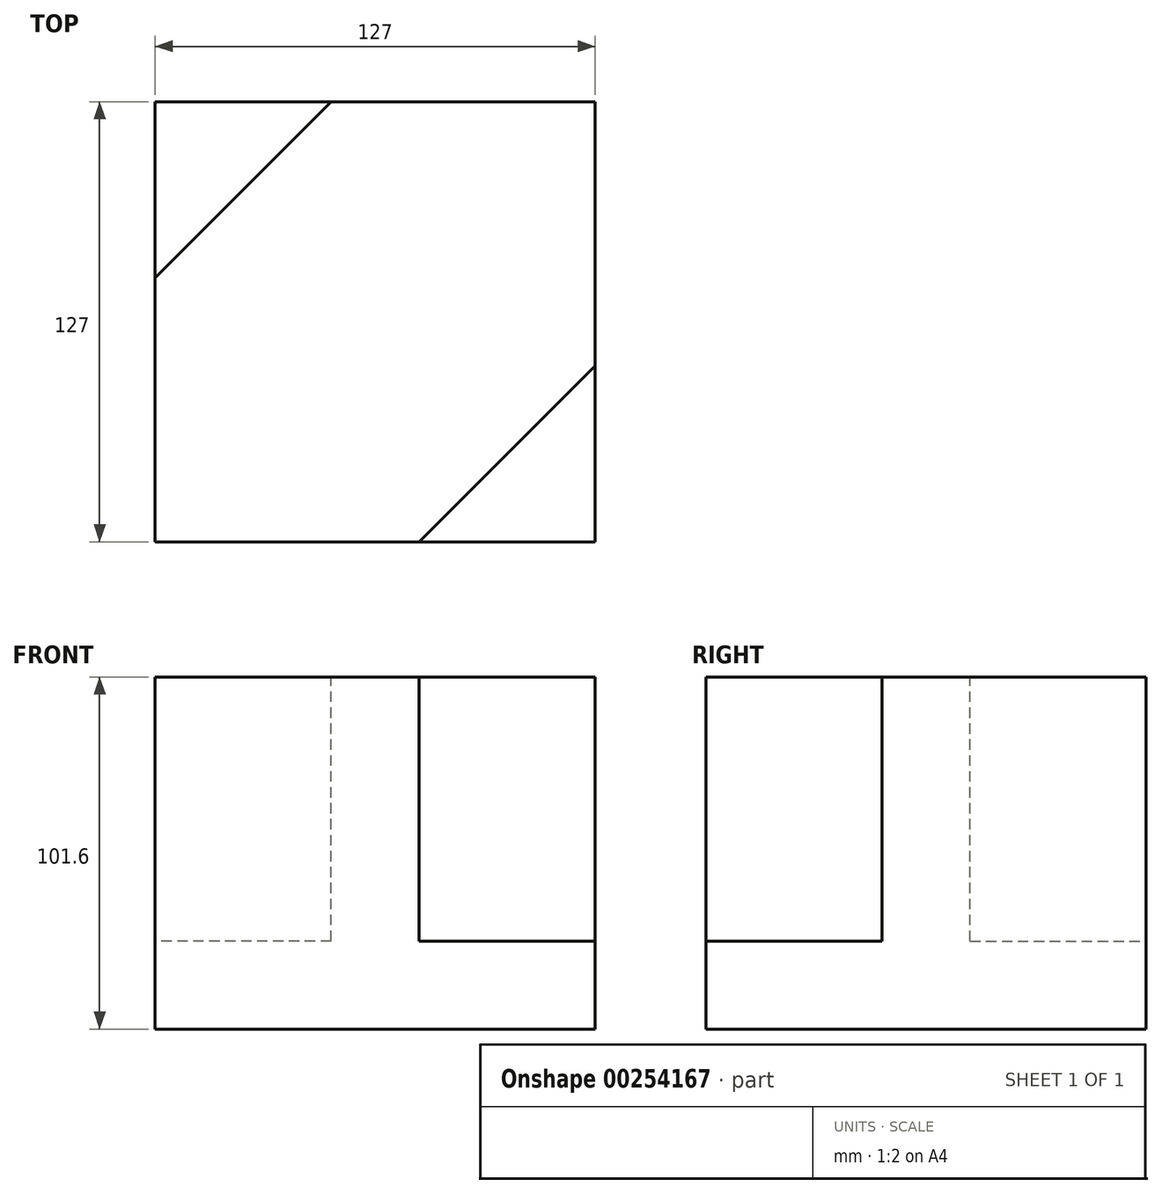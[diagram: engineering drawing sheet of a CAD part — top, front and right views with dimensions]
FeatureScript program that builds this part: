
annotation { "Feature Type Name" : "Feature", "Feature Type Description" : "" }
export const myFeature = defineFeature(function(context is Context, id is Id, definition is map)
    precondition{}
    {
        {
            var Q0;
            Q0=qCreatedBy(makeId("Front.planeOp"),FACE);
            var sketch = newSketch(context, id + "F0", { "sketchPlane" : qUnion([Q0])});
            skLineSegment(sketch, "E0.bottom", {"start": v(63.5, -50.8) * mm, "end": v(-63.5, -50.8) * mm});
            skLineSegment(sketch, "E0.top", {"start": v(63.5, 50.8) * mm, "end": v(-63.5, 50.8) * mm});
            skLineSegment(sketch, "E0.left", {"start": v(63.5, -50.8) * mm, "end": v(63.5, 50.8) * mm});
            skLineSegment(sketch, "E0.right", {"start": v(-63.5, -50.8) * mm, "end": v(-63.5, 50.8) * mm});
            skPoint(sketch, "E0.middle", {"position": v(0, 0) * mm});
            skSolve(sketch);
        }
        {
            var Q0;
            Q0=makeQuery(id+"F0.imprint","IMPRINT",FACE,{"disambiguationData":[TD([[makeQuery(id+"F0.imprint","IMPRINT",EDGE,{"derivedFrom":sQuery(id+"F0.wireOp",EDGE,"E0.bottom")}),-1.0]])]});
            extrude(context, id + "F1", {"entities" : qUnion([Q0]), "endBound" : BoundingType.SYMMETRIC, "depth" : 127 * mm});
        }
        {
            var Q0;
            Q0=makeQuery(id+"F1.opExtrude","SWEPT_FACE",FACE,{"disambiguationData":[OSD([sQuery(id+"F0.wireOp",EDGE,"E0.top")])]});
            var sketch = newSketch(context, id + "F2", { "sketchPlane" : qUnion([Q0])});
            skLineSegment(sketch, "E1", {"start": v(-63.5, -63.5) * mm, "end": v(63.5, 63.5) * mm, "construction": true});
            skLineSegment(sketch, "E2", {"start": v(-63.5, 63.5) * mm, "end": v(-12.7, 63.5) * mm});
            skLineSegment(sketch, "E3", {"start": v(-12.7, 63.5) * mm, "end": v(-63.5, 12.7) * mm});
            skLineSegment(sketch, "E4", {"start": v(-63.5, 12.7) * mm, "end": v(-63.5, 63.5) * mm});
            skLineSegment(sketch, "E5", {"start": v(63.5, -63.5) * mm, "end": v(12.7, -63.5) * mm});
            skLineSegment(sketch, "E6", {"start": v(12.7, -63.5) * mm, "end": v(63.5, -12.7) * mm});
            skLineSegment(sketch, "E7", {"start": v(63.5, -12.7) * mm, "end": v(63.5, -63.5) * mm});
            skSolve(sketch);
        }
        {
            var Q0;
            Q0=makeQuery(id+"F2.imprint","IMPRINT",FACE,{"disambiguationData":[TD([[makeQuery(id+"F2.imprint","IMPRINT",EDGE,{"derivedFrom":sQuery(id+"F2.wireOp",EDGE,"E2")}),1.0]])]});
            extrude(context, id + "F3", {"entities" : qUnion([Q0]), "operationType" : NewBodyOperationType.REMOVE, "oppositeDirection" : true, "depth" : 76.2 * mm});
        }
        {
            var Q0;
            Q0=makeQuery(id+"F2.imprint","IMPRINT",FACE,{"disambiguationData":[TD([[makeQuery(id+"F2.imprint","IMPRINT",EDGE,{"derivedFrom":sQuery(id+"F2.wireOp",EDGE,"E5")}),-1.0]])]});
            extrude(context, id + "F4", {"entities" : qUnion([Q0]), "operationType" : NewBodyOperationType.REMOVE, "oppositeDirection" : true, "depth" : 76.2 * mm});
        }
    });
